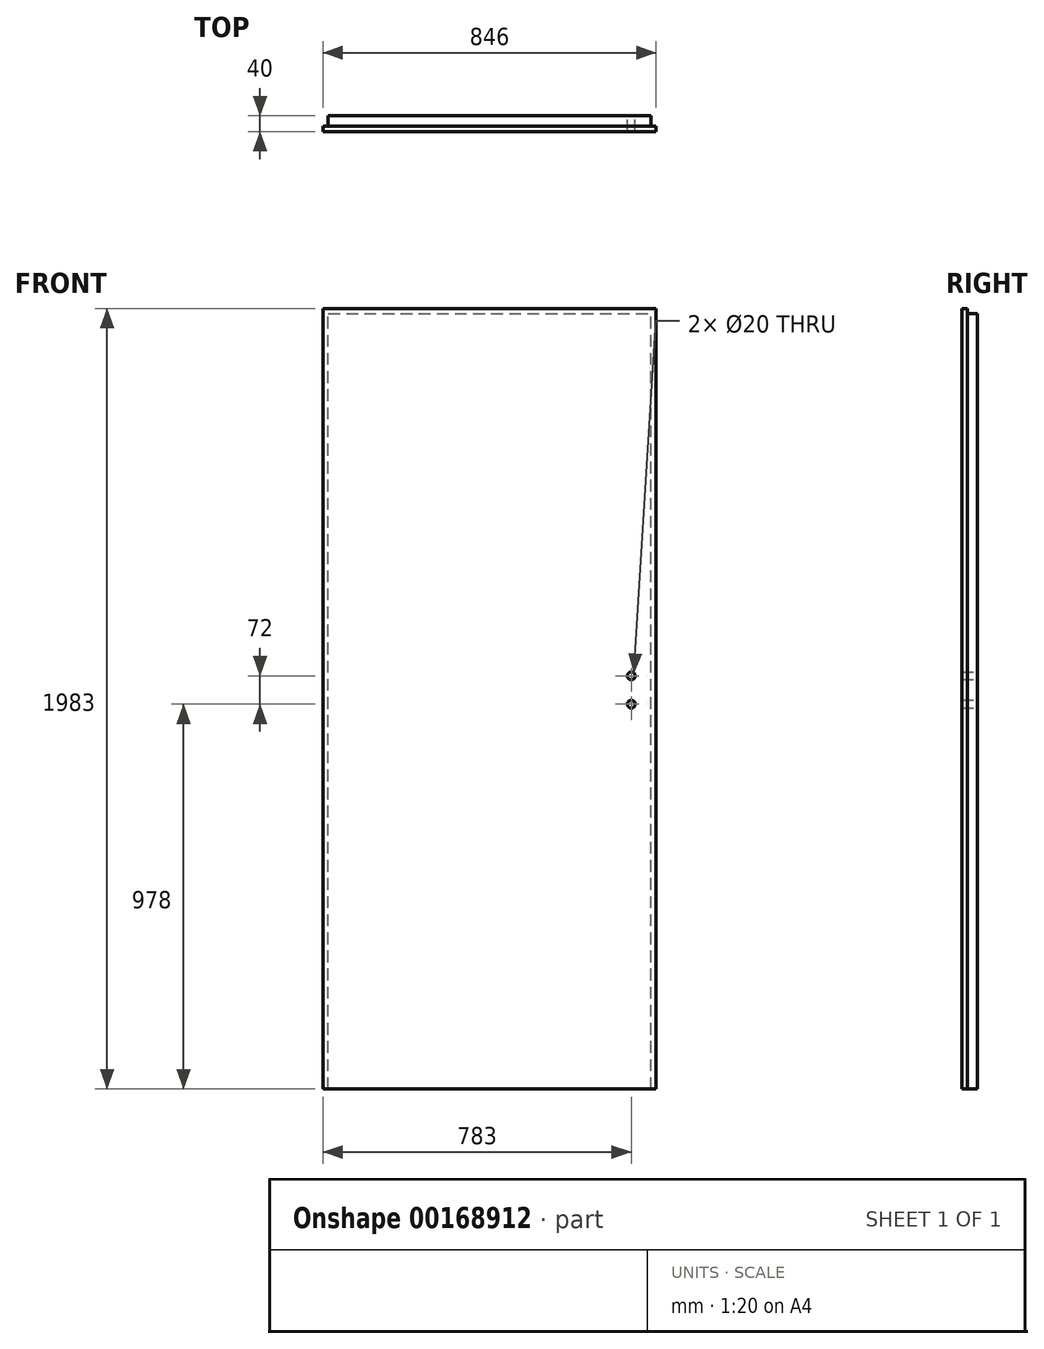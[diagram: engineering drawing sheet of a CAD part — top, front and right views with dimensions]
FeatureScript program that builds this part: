
annotation { "Feature Type Name" : "Feature", "Feature Type Description" : "" }
export const myFeature = defineFeature(function(context is Context, id is Id, definition is map)
    precondition{}
    {
        {
            var Q0;
            Q0=qCreatedBy(makeId("Top.planeOp"),FACE);
            var sketch = newSketch(context, id + "F0", { "sketchPlane" : qUnion([Q0])});
            skLineSegment(sketch, "E0.bottom", {"start": v(-423, -20) * mm, "end": v(423, -20) * mm});
            skLineSegment(sketch, "E0.top", {"start": v(-410, 20) * mm, "end": v(410, 20) * mm});
            skLineSegment(sketch, "E0.left", {"start": v(-423, -20) * mm, "end": v(-423, -6) * mm});
            skLineSegment(sketch, "E0.right", {"start": v(423, -20) * mm, "end": v(423, -6) * mm});
            skPoint(sketch, "E0.middle", {"position": v(0, 0) * mm});
            skLineSegment(sketch, "E1", {"start": v(0, 106.81) * mm, "end": v(0, -115.03) * mm, "construction": true});
            skLineSegment(sketch, "E2.top", {"start": v(-423, -6) * mm, "end": v(-410, -6) * mm, "construction": true});
            skLineSegment(sketch, "E2.right", {"start": v(-410, 20) * mm, "end": v(-410, -6) * mm, "construction": true});
            skPoint(sketch, "E3.orphan", {"position": v(-423, 20) * mm});
            skLineSegment(sketch, "E4", {"start": v(-410, 20) * mm, "end": v(-410, -6) * mm});
            skLineSegment(sketch, "E5", {"start": v(-410, -6) * mm, "end": v(-423, -6) * mm});
            skLineSegment(sketch, "E6.MirrorCS", {"start": v(410, 20) * mm, "end": v(410, -6) * mm, "construction": true});
            skLineSegment(sketch, "E7.MirrorCS", {"start": v(423, -6) * mm, "end": v(410, -6) * mm, "construction": true});
            skLineSegment(sketch, "E8", {"start": v(410, 20) * mm, "end": v(410, -6) * mm});
            skLineSegment(sketch, "E9", {"start": v(423, -6) * mm, "end": v(410, -6) * mm});
            skSolve(sketch);
        }
        {
            var Q0;
            Q0=makeQuery(id+"F0.imprint","IMPRINT",FACE,{"disambiguationData":[TD([[makeQuery(id+"F0.imprint","IMPRINT",EDGE,{"derivedFrom":sQuery(id+"F0.wireOp",EDGE,"E0.bottom")}),1.0]])]});
            extrude(context, id + "F1", {"entities" : qUnion([Q0]), "endBound" : BoundingType.SYMMETRIC, "oppositeDirection" : true, "depth" : 1983 * mm});
        }
        {
            var Q0;
            Q0=makeQuery(id+"F1.opExtrude","CAP_FACE",FACE,{"disambiguationData":[OSD([sQuery(id+"F0.wireOp",EDGE,"E0.bottom"),sQuery(id+"F0.wireOp",EDGE,"E0.top"),sQuery(id+"F0.wireOp",EDGE,"E0.left"),sQuery(id+"F0.wireOp",EDGE,"E0.right"),sQuery(id+"F0.wireOp",EDGE,"E4"),sQuery(id+"F0.wireOp",EDGE,"E5"),sQuery(id+"F0.wireOp",EDGE,"E8"),sQuery(id+"F0.wireOp",EDGE,"E9")])],"isStart":true});
            var sketch = newSketch(context, id + "F2", { "sketchPlane" : qUnion([Q0])});
            skLineSegment(sketch, "E10.bottom", {"start": v(-410, 20) * mm, "end": v(410, 20) * mm});
            skLineSegment(sketch, "E10.top", {"start": v(-410, -6) * mm, "end": v(410, -6) * mm});
            skLineSegment(sketch, "E10.left", {"start": v(-410, 20) * mm, "end": v(-410, -6) * mm});
            skLineSegment(sketch, "E10.right", {"start": v(410, 20) * mm, "end": v(410, -6) * mm});
            skSolve(sketch);
        }
        {
            var Q0;
            Q0 = qSketchRegion(id + "F2", true);
            extrude(context, id + "F3", {"entities" : qUnion([Q0]), "operationType" : NewBodyOperationType.REMOVE, "oppositeDirection" : true, "depth" : 13 * mm});
        }
        {
            var Q0;
            Q0=makeQuery(id+"F1.opExtrude","SWEPT_FACE",FACE,{"disambiguationData":[OSD([sQuery(id+"F0.wireOp",EDGE,"E0.top")])]});
            var sketch = newSketch(context, id + "F4", { "sketchPlane" : qUnion([Q0])});
            skCircle(sketch, "E11", {"center": v(-360, 58.5) * mm, "radius": 10 * mm});
            skCircle(sketch, "E12", {"center": v(-360, -13.5) * mm, "radius": 10 * mm});
            skSolve(sketch);
        }
        {
            var Q0;
            Q0 = qSketchRegion(id + "F4", true);
            extrude(context, id + "F5", {"entities" : qUnion([Q0]), "operationType" : NewBodyOperationType.REMOVE, "endBound" : BoundingType.UP_TO_NEXT, "oppositeDirection" : true, "depth" : 25 * mm});
        }
    });
